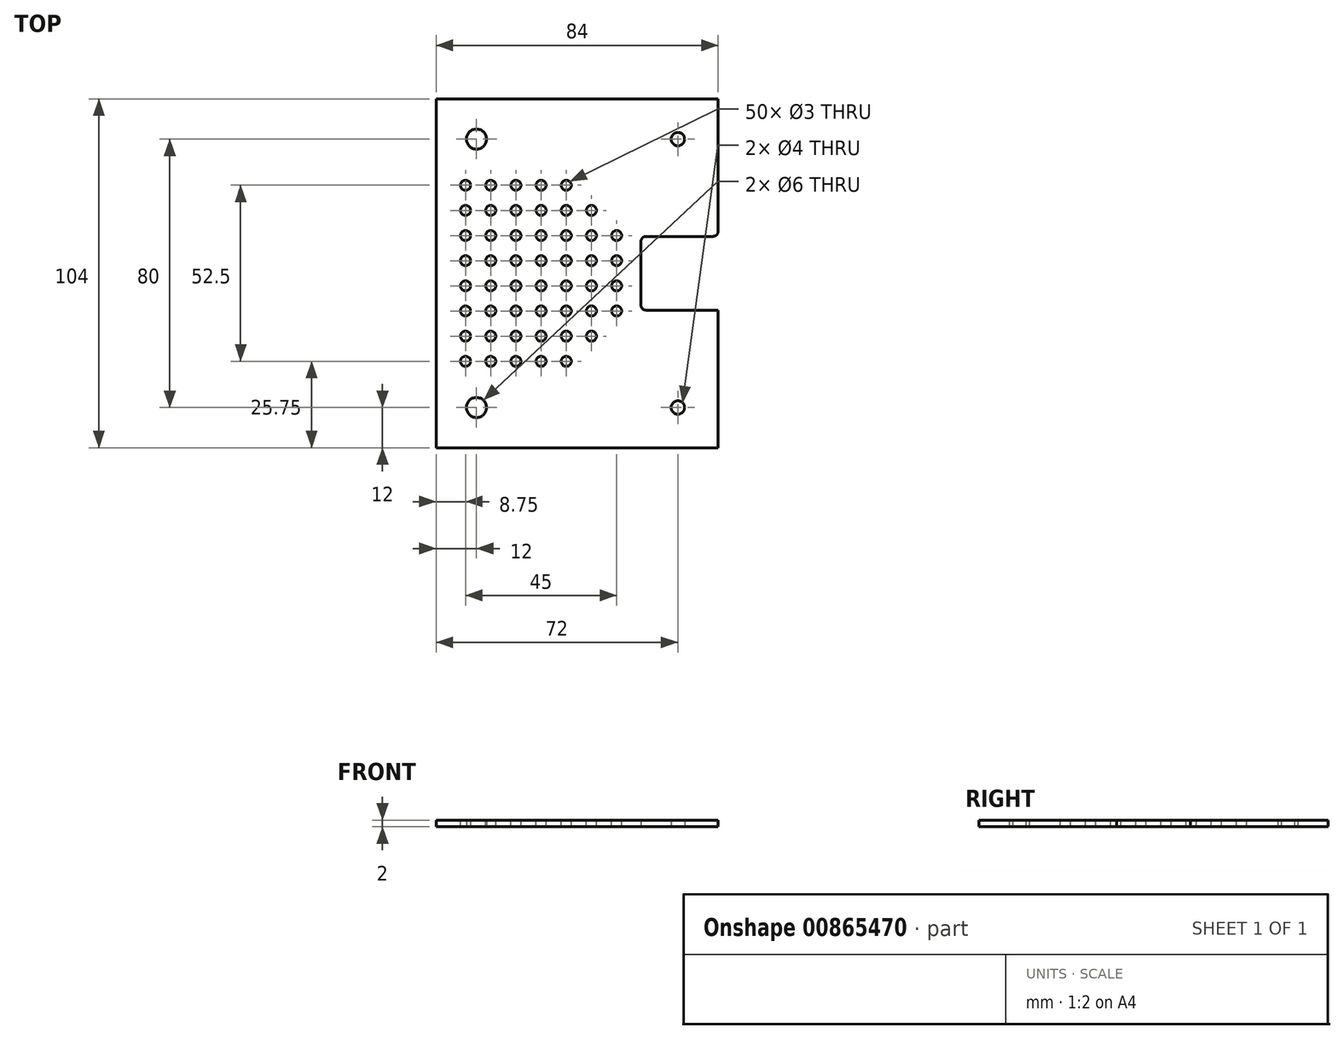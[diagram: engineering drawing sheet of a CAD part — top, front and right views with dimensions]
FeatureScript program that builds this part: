
annotation { "Feature Type Name" : "Feature", "Feature Type Description" : "" }
export const myFeature = defineFeature(function(context is Context, id is Id, definition is map)
    precondition{}
    {
        {
            var Q0;
            Q0=qCreatedBy(makeId("Top.planeOp"),FACE);
            var sketch = newSketch(context, id + "F0", { "sketchPlane" : qUnion([Q0])});
            skLineSegment(sketch, "E0.bottom", {"start": v(42, 52) * mm, "end": v(-42, 52) * mm});
            skLineSegment(sketch, "E0.top", {"start": v(42, -52) * mm, "end": v(-42, -52) * mm});
            skLineSegment(sketch, "E0.left", {"start": v(42, 52) * mm, "end": v(42, -52) * mm});
            skLineSegment(sketch, "E0.right", {"start": v(-42, 52) * mm, "end": v(-42, -52) * mm});
            skPoint(sketch, "E0.middle", {"position": v(0, 0) * mm});
            skCircle(sketch, "E1", {"center": v(-30, 40) * mm, "radius": 3 * mm});
            skCircle(sketch, "E2", {"center": v(30, 40) * mm, "radius": 2 * mm});
            skCircle(sketch, "E3", {"center": v(30, -40) * mm, "radius": 2 * mm});
            skCircle(sketch, "E4", {"center": v(-30, -40) * mm, "radius": 3 * mm});
            skSolve(sketch);
        }
        {
            var Q0;
            Q0 = qSketchRegion(id + "F0", true);
            extrude(context, id + "F1", {"entities" : qUnion([Q0]), "depth" : 2 * mm, "offsetDistance" : 25 * mm});
        }
        {
            var Q0;
            Q0=makeQuery(id+"F1.opExtrude","CAP_FACE",FACE,{"disambiguationData":[OSD([sQuery(id+"F0.wireOp",EDGE,"E0.bottom"),sQuery(id+"F0.wireOp",EDGE,"E0.top"),sQuery(id+"F0.wireOp",EDGE,"E0.left"),sQuery(id+"F0.wireOp",EDGE,"E0.right"),sQuery(id+"F0.wireOp",EDGE,"E1"),sQuery(id+"F0.wireOp",EDGE,"E2"),sQuery(id+"F0.wireOp",EDGE,"E3"),sQuery(id+"F0.wireOp",EDGE,"E4")])],"isStart":true});
            var sketch = newSketch(context, id + "F2", { "sketchPlane" : qUnion([Q0])});
            skLineSegment(sketch, "E5.bottom", {"start": v(42, -11) * mm, "end": v(19, -11) * mm});
            skLineSegment(sketch, "E5.top", {"start": v(42, 11) * mm, "end": v(19, 11) * mm});
            skLineSegment(sketch, "E5.left", {"start": v(42, -11) * mm, "end": v(42, 11) * mm});
            skLineSegment(sketch, "E5.right", {"start": v(19, -11) * mm, "end": v(19, 11) * mm});
            skPoint(sketch, "E5.middle", {"position": v(30.5, 0) * mm});
            skSolve(sketch);
        }
        {
            var Q0;
            Q0 = qSketchRegion(id + "F2", true);
            extrude(context, id + "F3", {"entities" : qUnion([Q0]), "operationType" : NewBodyOperationType.REMOVE, "endBound" : BoundingType.THROUGH_ALL, "oppositeDirection" : true, "depth" : 25 * mm, "offsetDistance" : 25 * mm});
        }
        {
            var Q0;
            Q0=makeQuery(id+"F3.boolean.opBoolean","COPY",EDGE,{"derivedFrom":makeQuery(id+"F3.opExtrude","SWEPT_EDGE",EDGE,{"disambiguationData":[OSD([sQuery(id+"F2.wireOp",EDGE,"E5.bottom"),sQuery(id+"F2.wireOp",EDGE,"E5.right")])]})});
            var Q1;
            Q1=makeQuery(id+"F3.boolean.opBoolean","COPY",EDGE,{"derivedFrom":makeQuery(id+"F3.opExtrude","SWEPT_EDGE",EDGE,{"disambiguationData":[OSD([sQuery(id+"F0.wireOp",EDGE,"E0.left"),sQuery(id+"F2.wireOp",EDGE,"E5.bottom"),sQuery(id+"F2.wireOp",EDGE,"E5.left")])]})});
            var Q2;
            Q2=makeQuery(id+"F3.boolean.opBoolean","COPY",EDGE,{"derivedFrom":makeQuery(id+"F3.opExtrude","SWEPT_EDGE",EDGE,{"disambiguationData":[OSD([sQuery(id+"F2.wireOp",EDGE,"E5.top"),sQuery(id+"F2.wireOp",EDGE,"E5.right")])]})});
            var Q3;
            Q3=makeQuery(id+"F3.boolean.opBoolean","COPY",EDGE,{"derivedFrom":makeQuery(id+"F3.opExtrude","SWEPT_EDGE",EDGE,{"disambiguationData":[OSD([sQuery(id+"F0.wireOp",EDGE,"E0.left"),sQuery(id+"F2.wireOp",EDGE,"E5.top"),sQuery(id+"F2.wireOp",EDGE,"E5.left")])]})});
            fillet(context, id + "F4", {"entities" : qUnion([Q0, Q1, Q2, Q3]), "radius" : 1.5 * mm, "tangentPropagation" : true, "allowEdgeOverflow" : false});
        }
        {
            var Q0;
            Q0=makeQuery(id+"F1.opExtrude","CAP_FACE",FACE,{"disambiguationData":[OSD([sQuery(id+"F0.wireOp",EDGE,"E0.bottom"),sQuery(id+"F0.wireOp",EDGE,"E0.top"),sQuery(id+"F0.wireOp",EDGE,"E0.left"),sQuery(id+"F0.wireOp",EDGE,"E0.right"),sQuery(id+"F0.wireOp",EDGE,"E1"),sQuery(id+"F0.wireOp",EDGE,"E2"),sQuery(id+"F0.wireOp",EDGE,"E3"),sQuery(id+"F0.wireOp",EDGE,"E4")])],"isStart":false});
            var sketch = newSketch(context, id + "F5", { "sketchPlane" : qUnion([Q0])});
            skCircle(sketch, "E6", {"center": v(-33.25, -26.25) * mm, "radius": 1.5 * mm});
            skCircle(sketch, "E7.0.1.0", {"center": v(-33.25, -18.75) * mm, "radius": 1.5 * mm});
            skCircle(sketch, "E7.0.2.0", {"center": v(-33.25, -11.25) * mm, "radius": 1.5 * mm});
            skCircle(sketch, "E7.0.3.0", {"center": v(-33.25, -3.75) * mm, "radius": 1.5 * mm});
            skCircle(sketch, "E7.1.0.0", {"center": v(-25.75, -26.25) * mm, "radius": 1.5 * mm});
            skCircle(sketch, "E7.1.1.0", {"center": v(-25.75, -18.75) * mm, "radius": 1.5 * mm});
            skCircle(sketch, "E7.1.2.0", {"center": v(-25.75, -11.25) * mm, "radius": 1.5 * mm});
            skCircle(sketch, "E7.1.3.0", {"center": v(-25.75, -3.75) * mm, "radius": 1.5 * mm});
            skCircle(sketch, "E7.2.0.0", {"center": v(-18.25, -26.25) * mm, "radius": 1.5 * mm});
            skCircle(sketch, "E7.2.1.0", {"center": v(-18.25, -18.75) * mm, "radius": 1.5 * mm});
            skCircle(sketch, "E7.2.2.0", {"center": v(-18.25, -11.25) * mm, "radius": 1.5 * mm});
            skCircle(sketch, "E7.2.3.0", {"center": v(-18.25, -3.75) * mm, "radius": 1.5 * mm});
            skCircle(sketch, "E7.3.0.0", {"center": v(-10.75, -26.25) * mm, "radius": 1.5 * mm});
            skCircle(sketch, "E7.3.1.0", {"center": v(-10.75, -18.75) * mm, "radius": 1.5 * mm});
            skCircle(sketch, "E7.3.2.0", {"center": v(-10.75, -11.25) * mm, "radius": 1.5 * mm});
            skCircle(sketch, "E7.3.3.0", {"center": v(-10.75, -3.75) * mm, "radius": 1.5 * mm});
            skCircle(sketch, "E7.4.0.0", {"center": v(-3.25, -26.25) * mm, "radius": 1.5 * mm});
            skCircle(sketch, "E7.4.1.0", {"center": v(-3.25, -18.75) * mm, "radius": 1.5 * mm});
            skCircle(sketch, "E7.4.2.0", {"center": v(-3.25, -11.25) * mm, "radius": 1.5 * mm});
            skCircle(sketch, "E7.4.3.0", {"center": v(-3.25, -3.75) * mm, "radius": 1.5 * mm});
            skCircle(sketch, "E7.5.1.0", {"center": v(4.25, -18.75) * mm, "radius": 1.5 * mm});
            skCircle(sketch, "E7.5.2.0", {"center": v(4.25, -11.25) * mm, "radius": 1.5 * mm});
            skCircle(sketch, "E7.5.3.0", {"center": v(4.25, -3.75) * mm, "radius": 1.5 * mm});
            skCircle(sketch, "E7.6.2.0", {"center": v(11.75, -11.25) * mm, "radius": 1.5 * mm});
            skCircle(sketch, "E7.6.3.0", {"center": v(11.75, -3.75) * mm, "radius": 1.5 * mm});
            skLineSegment(sketch, "E7.direction1", {"start": v(-33.25, -26.25) * mm, "end": v(-25.75, -26.25) * mm, "construction": true});
            skLineSegment(sketch, "E7.direction2", {"start": v(-33.25, -26.25) * mm, "end": v(-33.25, -18.75) * mm, "construction": true});
            skCircle(sketch, "E8.MirrorC", {"center": v(-33.25, 26.25) * mm, "radius": 1.5 * mm});
            skCircle(sketch, "E9.MirrorC", {"center": v(-25.75, 26.25) * mm, "radius": 1.5 * mm});
            skCircle(sketch, "E10.MirrorC", {"center": v(-25.75, 3.75) * mm, "radius": 1.5 * mm});
            skCircle(sketch, "E11.MirrorC", {"center": v(-3.25, 3.75) * mm, "radius": 1.5 * mm});
            skCircle(sketch, "E12.MirrorC", {"center": v(-10.75, 26.25) * mm, "radius": 1.5 * mm});
            skCircle(sketch, "E13.MirrorC", {"center": v(-3.25, 26.25) * mm, "radius": 1.5 * mm});
            skCircle(sketch, "E14.MirrorC", {"center": v(-33.25, 3.75) * mm, "radius": 1.5 * mm});
            skCircle(sketch, "E15.MirrorC", {"center": v(-10.75, 3.75) * mm, "radius": 1.5 * mm});
            skCircle(sketch, "E16.MirrorC", {"center": v(-33.25, 18.75) * mm, "radius": 1.5 * mm});
            skCircle(sketch, "E17.MirrorC", {"center": v(-18.25, 3.75) * mm, "radius": 1.5 * mm});
            skCircle(sketch, "E18.MirrorC", {"center": v(-18.25, 18.75) * mm, "radius": 1.5 * mm});
            skCircle(sketch, "E19.MirrorC", {"center": v(-25.75, 11.25) * mm, "radius": 1.5 * mm});
            skCircle(sketch, "E20.MirrorC", {"center": v(11.75, 11.25) * mm, "radius": 1.5 * mm});
            skCircle(sketch, "E21.MirrorC", {"center": v(-25.75, 18.75) * mm, "radius": 1.5 * mm});
            skCircle(sketch, "E22.MirrorC", {"center": v(-10.75, 18.75) * mm, "radius": 1.5 * mm});
            skCircle(sketch, "E23.MirrorC", {"center": v(-33.25, 11.25) * mm, "radius": 1.5 * mm});
            skCircle(sketch, "E24.MirrorC", {"center": v(-3.25, 18.75) * mm, "radius": 1.5 * mm});
            skCircle(sketch, "E25.MirrorC", {"center": v(4.25, 18.75) * mm, "radius": 1.5 * mm});
            skCircle(sketch, "E26.MirrorC", {"center": v(-10.75, 11.25) * mm, "radius": 1.5 * mm});
            skCircle(sketch, "E27.MirrorC", {"center": v(11.75, 3.75) * mm, "radius": 1.5 * mm});
            skCircle(sketch, "E28.MirrorC", {"center": v(-18.25, 26.25) * mm, "radius": 1.5 * mm});
            skCircle(sketch, "E29.MirrorC", {"center": v(4.25, 3.75) * mm, "radius": 1.5 * mm});
            skCircle(sketch, "E30.MirrorC", {"center": v(-3.25, 11.25) * mm, "radius": 1.5 * mm});
            skLineSegment(sketch, "E31.MirrorCS", {"start": v(-33.25, 26.25) * mm, "end": v(-33.25, 18.75) * mm, "construction": true});
            skLineSegment(sketch, "E32.MirrorCS", {"start": v(-33.25, 26.25) * mm, "end": v(-25.75, 26.25) * mm, "construction": true});
            skCircle(sketch, "E33.MirrorC", {"center": v(4.25, 11.25) * mm, "radius": 1.5 * mm});
            skCircle(sketch, "E34.MirrorC", {"center": v(-18.25, 11.25) * mm, "radius": 1.5 * mm});
            skSolve(sketch);
        }
        {
            var Q0;
            Q0 = qSketchRegion(id + "F5", true);
            extrude(context, id + "F6", {"entities" : qUnion([Q0]), "operationType" : NewBodyOperationType.REMOVE, "endBound" : BoundingType.THROUGH_ALL, "oppositeDirection" : true, "depth" : 25 * mm, "offsetDistance" : 25 * mm});
        }
    });
